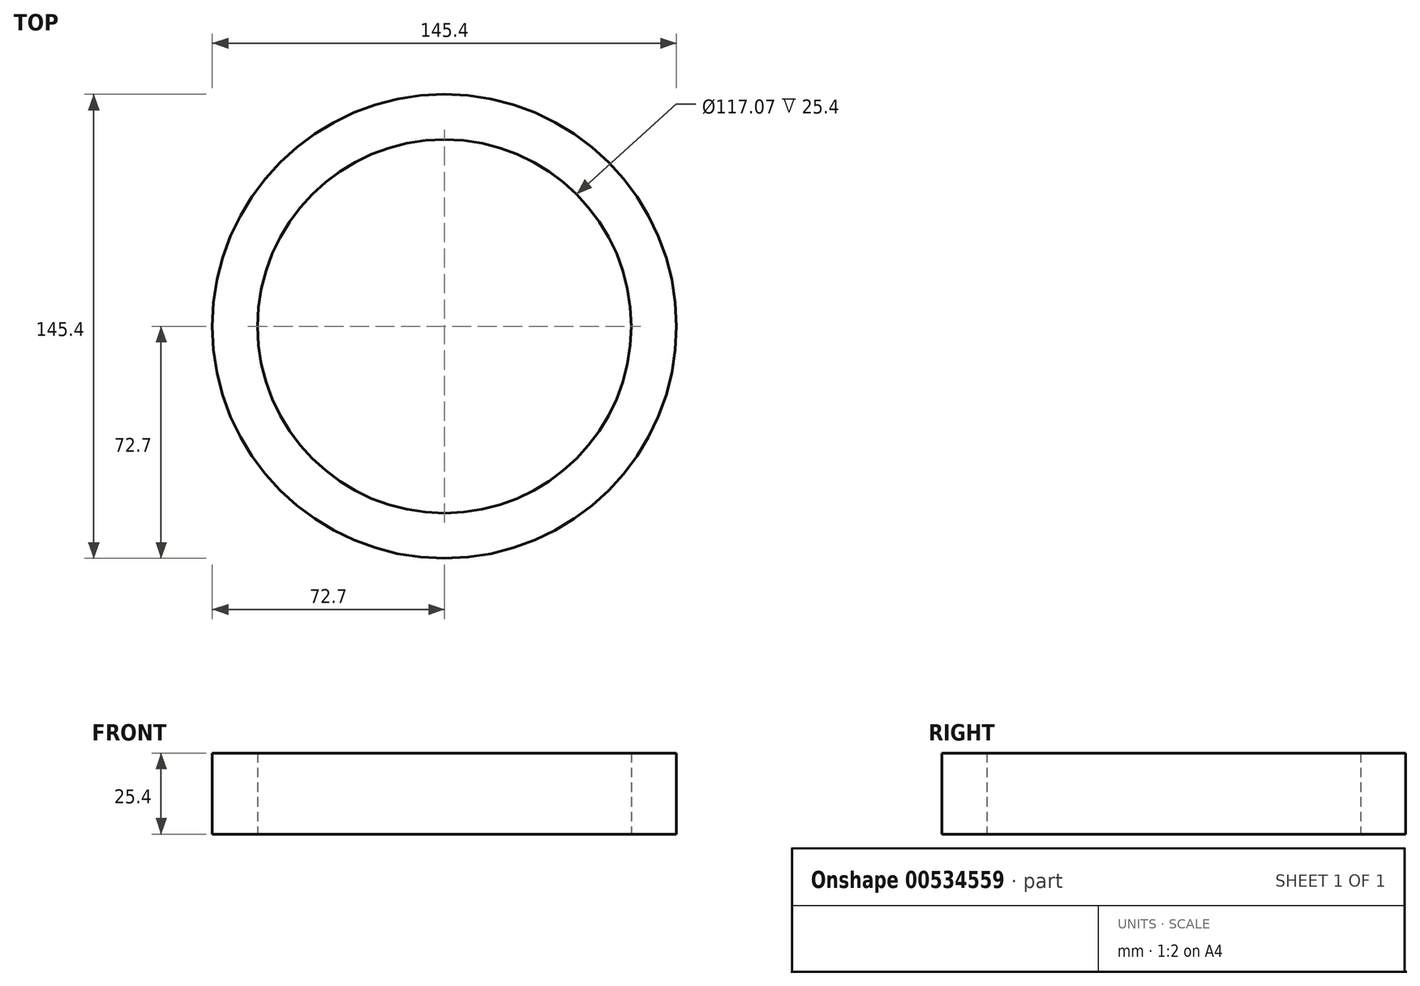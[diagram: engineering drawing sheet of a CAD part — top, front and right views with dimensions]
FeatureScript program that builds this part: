
annotation { "Feature Type Name" : "Feature", "Feature Type Description" : "" }
export const myFeature = defineFeature(function(context is Context, id is Id, definition is map)
    precondition{}
    {
        {
            var Q0;
            Q0=qCreatedBy(makeId("Top.planeOp"),FACE);
            var sketch = newSketch(context, id + "F0", { "sketchPlane" : qUnion([Q0])});
            skCircle(sketch, "E0", {"center": v(0, 0) * mm, "radius": 12.5 * mm});
            skCircle(sketch, "E1", {"center": v(0, 0) * mm, "radius": 26.28 * mm});
            skCircle(sketch, "E2", {"center": v(0, 0) * mm, "radius": 42.23 * mm});
            skCircle(sketch, "E3", {"center": v(0, 0) * mm, "radius": 58.53 * mm});
            skCircle(sketch, "E4", {"center": v(0, 0) * mm, "radius": 72.7 * mm});
            skSolve(sketch);
        }
        {
            var Q0;
            Q0 = qSketchRegion(id + "F0", true);
            extrude(context, id + "F1", {"entities" : qUnion([Q0]), "depth" : 25.4 * mm, "offsetDistance" : 25.4 * mm});
        }
    });
